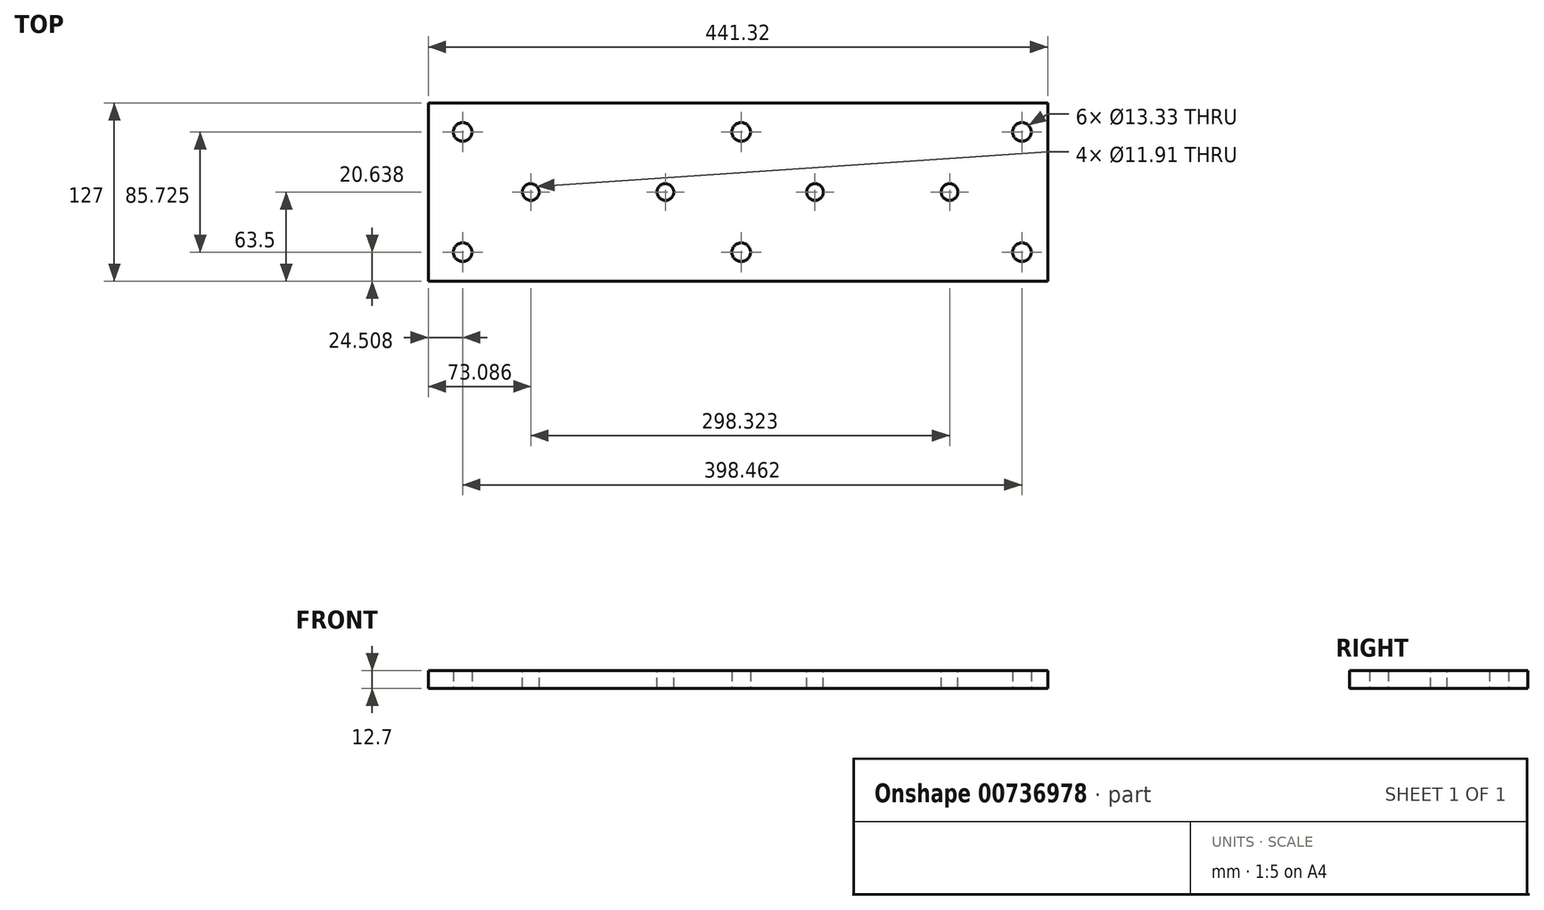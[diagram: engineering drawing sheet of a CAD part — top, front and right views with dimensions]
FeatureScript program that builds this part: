
annotation { "Feature Type Name" : "Feature", "Feature Type Description" : "" }
export const myFeature = defineFeature(function(context is Context, id is Id, definition is map)
    precondition{}
    {
        {
            var Q0;
            Q0=qCreatedBy(makeId("Top.planeOp"),FACE);
            var sketch = newSketch(context, id + "F0", { "sketchPlane" : qUnion([Q0])});
            skLineSegment(sketch, "E0.bottom", {"start": v(-220.66, 63.5) * mm, "end": v(220.66, 63.5) * mm});
            skLineSegment(sketch, "E0.top", {"start": v(-220.66, -63.5) * mm, "end": v(220.66, -63.5) * mm});
            skLineSegment(sketch, "E0.left", {"start": v(-220.66, 63.5) * mm, "end": v(-220.66, -63.5) * mm});
            skLineSegment(sketch, "E0.right", {"start": v(220.66, 63.5) * mm, "end": v(220.66, -63.5) * mm});
            skLineSegment(sketch, "E1", {"start": v(-220.66, 0) * mm, "end": v(220.66, 0) * mm, "construction": true});
            skLineSegment(sketch, "E2", {"start": v(0, 63.5) * mm, "end": v(0, -63.5) * mm, "construction": true});
            skCircle(sketch, "E3", {"center": v(-196.15, 42.86) * mm, "radius": 6.67 * mm});
            skCircle(sketch, "E4", {"center": v(2.29, 42.86) * mm, "radius": 6.67 * mm});
            skCircle(sketch, "E5", {"center": v(202.31, 42.86) * mm, "radius": 6.67 * mm});
            skCircle(sketch, "E6", {"center": v(-196.15, -42.86) * mm, "radius": 6.67 * mm});
            skCircle(sketch, "E7", {"center": v(2.29, -42.86) * mm, "radius": 6.67 * mm});
            skCircle(sketch, "E8", {"center": v(202.31, -42.86) * mm, "radius": 6.67 * mm});
            skLineSegment(sketch, "E9", {"start": v(-196.15, 42.86) * mm, "end": v(-196.15, 0) * mm, "construction": true});
            skLineSegment(sketch, "E10", {"start": v(-196.15, 0) * mm, "end": v(-196.15, -42.86) * mm, "construction": true});
            skLineSegment(sketch, "E11", {"start": v(-51.69, 0) * mm, "end": v(54.86, 0) * mm, "construction": true});
            skPoint(sketch, "E12", {"position": v(-147.57, 0) * mm});
            skPoint(sketch, "E13", {"position": v(-51.69, 0) * mm});
            skPoint(sketch, "E14", {"position": v(54.86, 0) * mm});
            skPoint(sketch, "E15", {"position": v(150.75, 0) * mm});
            skSolve(sketch);
        }
        {
            var Q0;
            Q0 = qSketchRegion(id + "F0", true);
            extrude(context, id + "F1", {"entities" : qUnion([Q0]), "depth" : 12.7 * mm, "offsetDistance" : 25.4 * mm});
        }
        {
            var Q0;
            Q0=sQuery(id+"F0.wireOp",VERTEX,"E12");
            var Q1;
            Q1=sQuery(id+"F0.wireOp",VERTEX,"E13");
            var Q2;
            Q2=sQuery(id+"F0.wireOp",VERTEX,"E14");
            var Q3;
            Q3=sQuery(id+"F0.wireOp",VERTEX,"E15");
            var Q4;
            Q4=makeQuery(id+"F1.opExtrude","SWEPT_BODY",BODY,{"disambiguationData":[OSD([sQuery(id+"F0.wireOp",EDGE,"E0.bottom"),sQuery(id+"F0.wireOp",EDGE,"E0.top"),sQuery(id+"F0.wireOp",EDGE,"E0.left"),sQuery(id+"F0.wireOp",EDGE,"E0.right"),sQuery(id+"F0.wireOp",EDGE,"E3"),sQuery(id+"F0.wireOp",EDGE,"E4"),sQuery(id+"F0.wireOp",EDGE,"E5"),sQuery(id+"F0.wireOp",EDGE,"E6"),sQuery(id+"F0.wireOp",EDGE,"E7"),sQuery(id+"F0.wireOp",EDGE,"E8")])]});
            hole(context, id + "F2", {"style" : HoleStyle.SIMPLE, "endStyle" : HoleEndStyle.BLIND, "oppositeDirection" : true, "standardTappedOrClearance" : lookupTablePath({ "standard" : "ANSI", "engagement" : "75%", "pitch" : "28 tpi", "size" : "1/2", "type" : "Tapped" }), "standardBlindInLast" : lookupTablePath({ "standard" : "ANSI", "fit" : "Normal", "engagement" : "75%", "pitch" : "28 tpi", "size" : "1/2", "type" : "Clearance & tapped" }), "holeDiameter" : 11.9 * mm, "majorDiameter" : 12.7 * mm, "showTappedDepth" : true, "holeDepth" : 19.4 * mm, "isTappedThrough" : true, "tappedDepth" : 16.67 * mm, "tapClearance" : 3, "locations" : qUnion([Q0, Q1, Q2, Q3]), "scope" : qUnion([Q4]), "startStyle" : HoleStartStyle.PART});
        }
    });
